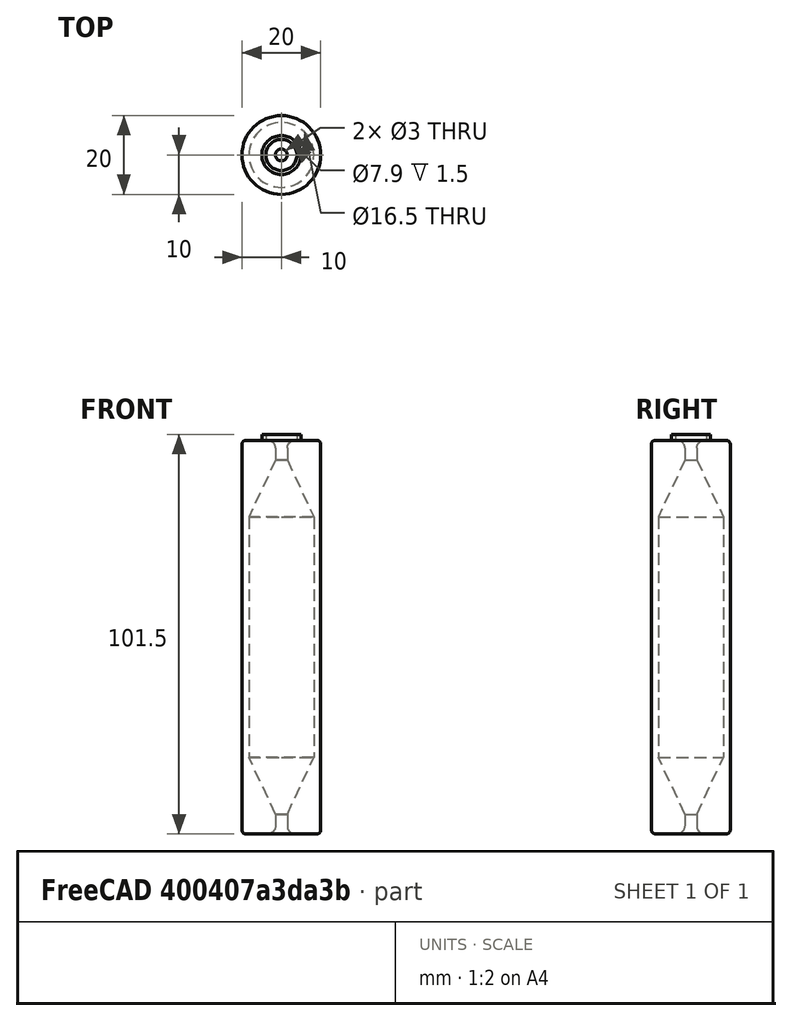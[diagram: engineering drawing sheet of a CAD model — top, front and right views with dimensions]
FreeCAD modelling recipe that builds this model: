
FCSTD DOCUMENT  (FreeCAD 0.14R3703 (Git))
Label: entretoise_1
License: CC-BY 3.0
LicenseURL: http://creativecommons.org/licenses/by/3.0/
objects: Sketcher::SketchObject×1, PartDesign::Revolution×1
note: 3 computed .brp shape members not serialized (recipe doc carries the construction recipe); baked Part::Feature solids carry a one-line shape summary decoded from their .brp

FEATURE [Sketcher::SketchObject] Sketch
  Placement = pos=(0,0,0) rot=(0.57735,0.57735,0.57735;2.0944rad)
  sketch-geometry (16):
    g0: LineSegment StartX=-1.5 StartY=5 StartZ=0 EndX=-1.5 EndY=2 EndZ=0
    g1: LineSegment StartX=-3.5 StartY=0 StartZ=0 EndX=-9 EndY=0 EndZ=0
    g2: LineSegment StartX=-10 StartY=1 StartZ=0 EndX=-10 EndY=99 EndZ=0
    g3: LineSegment StartX=-9 StartY=100 StartZ=0 EndX=-4.95 EndY=100 EndZ=0
    g4: LineSegment StartX=-1.5 StartY=98 StartZ=0 EndX=-1.5 EndY=95 EndZ=0
    g5: ArcOfCircle CenterX=-9 CenterY=99 CenterZ=0 NormalX=0 NormalY=0 NormalZ=1 Radius=1 StartAngle=1.5708 EndAngle=3.14159
    g6: ArcOfCircle CenterX=-3.5 CenterY=98 CenterZ=0 NormalX=0 NormalY=0 NormalZ=1 Radius=2 StartAngle=0 EndAngle=1.5708
    g7: ArcOfCircle CenterX=-9 CenterY=1 CenterZ=0 NormalX=0 NormalY=0 NormalZ=1 Radius=1 StartAngle=3.14159 EndAngle=4.71239
    g8: ArcOfCircle CenterX=-3.5 CenterY=2 CenterZ=0 NormalX=0 NormalY=0 NormalZ=1 Radius=2 StartAngle=4.71239 EndAngle=6.28319
    g9: LineSegment StartX=-4.95 StartY=100 StartZ=0 EndX=-4.95 EndY=101.5 EndZ=0
    g10: LineSegment StartX=-4.95 StartY=101.5 StartZ=0 EndX=-3.95 EndY=101.5 EndZ=0
    g11: LineSegment StartX=-3.95 StartY=101.5 StartZ=0 EndX=-3.95 EndY=100 EndZ=0
    g12: LineSegment StartX=-3.95 StartY=100 StartZ=0 EndX=-3.5 EndY=100 EndZ=0
    g13: LineSegment StartX=-1.5 StartY=95 StartZ=0 EndX=-8.25 EndY=80.5246 EndZ=0
    g14: LineSegment StartX=-1.5 StartY=5 StartZ=0 EndX=-8.25 EndY=19.4754 EndZ=0
    g15: LineSegment StartX=-8.25 StartY=80.5246 StartZ=0 EndX=-8.25 EndY=19.4754 EndZ=0
  constraints (46):
    c: Vertical(g0)
    c: Horizontal(g1)
    c: Vertical(g2)
    c: Vertical(g4)
    c: Horizontal(g3)
    c: Distance(g0,g1) = 5
    c: Distance(g4,g3) = 5
    c: Tangent(g2,g5)
    c: Tangent(g3,g5)
    c: Radius(g5) = 1
    c: Tangent(g4,g6)
    c: Tangent(g1,g7)
    c: Tangent(g2,g7)
    c: Radius(g7) = 1
    c: Tangent(g1,g8)
    c: Tangent(g0,g8)
    c: Radius(g8) = 2
    c: Distance(g3,g1) = 100
    c: DistanceX(g-2,g2) = -10
    c: DistanceX(g-2,g4) = -1.5
    c: DistanceX(g-2,g0) = -1.5
    c: PointOnObject(g1,g-1)
    c: Vertical(g9)
    c: PointOnObject(g10,g9)
    c: Horizontal(g10)
    c: Coincident(g10,g11)
    c: PointOnObject(g11,g3)
    c: Vertical(g11)
    c: Coincident(g12,g11)
    c: Coincident(g12,g6)
    c: Horizontal(g12)
    c: Coincident(g3,g9)
    c: DistanceX(g-2,g10) = -4.95
    c: Coincident(g9,g10)
    c: Distance(g9) = 1.5
    c: Distance(g10) = 1
    c: Coincident(g13,g4)
    c: Angle(g-2,g13) = 2.70526
    c: Coincident(g14,g0)
    c: Angle(g14,g0) = 2.70526
    c: Coincident(g15,g13)
    c: Coincident(g15,g14)
    c: Vertical(g15)
    c: Distance(g14,g2) = 1.75
    c: Tangent(g12,g6)
    c: Radius(g6) = 2
FEATURE [PartDesign::Revolution] Revolution  label="entretoise_1"
  Angle = 360
  Axis = (0,0,1)
  Base = (0,0,0)
  Placement = pos=(0,0,0) rot=(0.57735,0.57735,0.57735;2.0944rad)
  ReferenceAxis = -> Sketch [V_Axis]
  Sketch = -> Sketch
